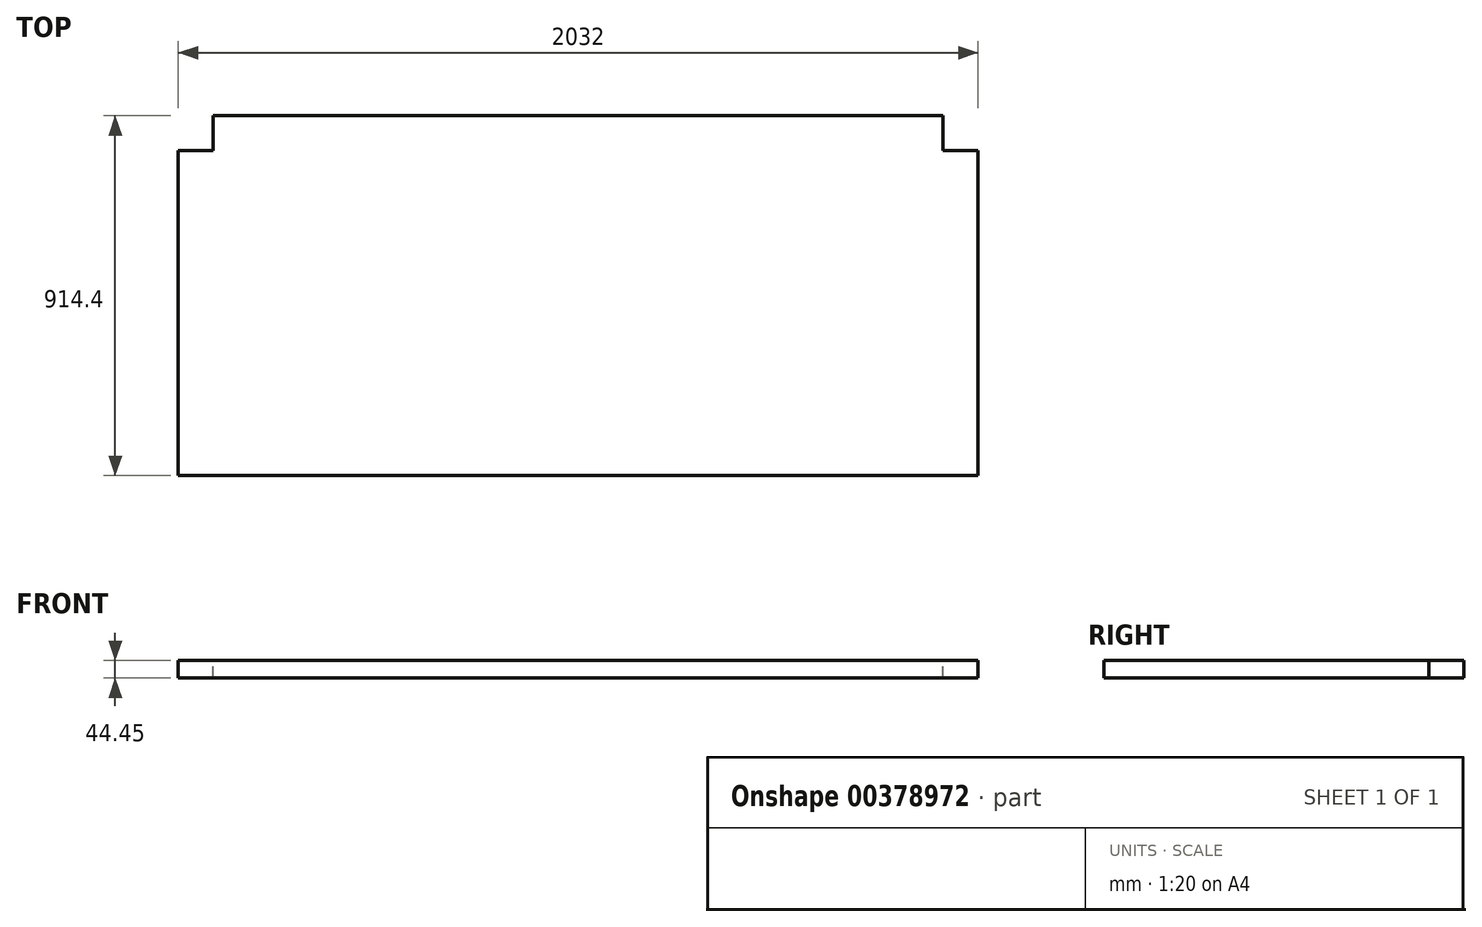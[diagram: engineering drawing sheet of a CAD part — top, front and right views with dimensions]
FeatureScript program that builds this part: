
annotation { "Feature Type Name" : "Feature", "Feature Type Description" : "" }
export const myFeature = defineFeature(function(context is Context, id is Id, definition is map)
    precondition{}
    {
        {
            var Q0;
            Q0=qCreatedBy(makeId("Top.planeOp"),FACE);
            var sketch = newSketch(context, id + "F0", { "sketchPlane" : qUnion([Q0])});
            skLineSegment(sketch, "E0.bottom", {"start": v(-999.24, 324.36) * mm, "end": v(1032.76, 324.36) * mm});
            skLineSegment(sketch, "E0.top", {"start": v(-999.24, -590.04) * mm, "end": v(1032.76, -590.04) * mm});
            skLineSegment(sketch, "E0.left", {"start": v(-999.24, 324.36) * mm, "end": v(-999.24, -590.04) * mm});
            skLineSegment(sketch, "E0.right", {"start": v(1032.76, 324.36) * mm, "end": v(1032.76, -590.04) * mm});
            skLineSegment(sketch, "E1.bottom", {"start": v(-999.24, 324.36) * mm, "end": v(-910.34, 324.36) * mm});
            skLineSegment(sketch, "E1.top", {"start": v(-999.24, 235.46) * mm, "end": v(-910.34, 235.46) * mm});
            skLineSegment(sketch, "E1.left", {"start": v(-999.24, 324.36) * mm, "end": v(-999.24, 235.46) * mm});
            skLineSegment(sketch, "E1.right", {"start": v(-910.34, 324.36) * mm, "end": v(-910.34, 235.46) * mm});
            skLineSegment(sketch, "E2.bottom", {"start": v(1032.76, 324.36) * mm, "end": v(943.86, 324.36) * mm});
            skLineSegment(sketch, "E2.top", {"start": v(1032.76, 235.46) * mm, "end": v(943.86, 235.46) * mm});
            skLineSegment(sketch, "E2.left", {"start": v(1032.76, 324.36) * mm, "end": v(1032.76, 235.46) * mm});
            skLineSegment(sketch, "E2.right", {"start": v(943.86, 324.36) * mm, "end": v(943.86, 235.46) * mm});
            skSolve(sketch);
        }
        {
            var Q0;
            {var subQ1=sQuery(id+"F0.wireOp",EDGE,"E0.top");Q0=makeQuery(id+"F0.imprint","IMPRINT",FACE,{"disambiguationData":[TD([[makeQuery(id+"F0.imprint","IMPRINT",EDGE,{"derivedFrom":subQ1}),1.0]])]});}
            extrude(context, id + "F1", {"entities" : qUnion([Q0]), "oppositeDirection" : true, "depth" : 44.45 * mm, "offsetDistance" : 25.4 * mm});
        }
    });
